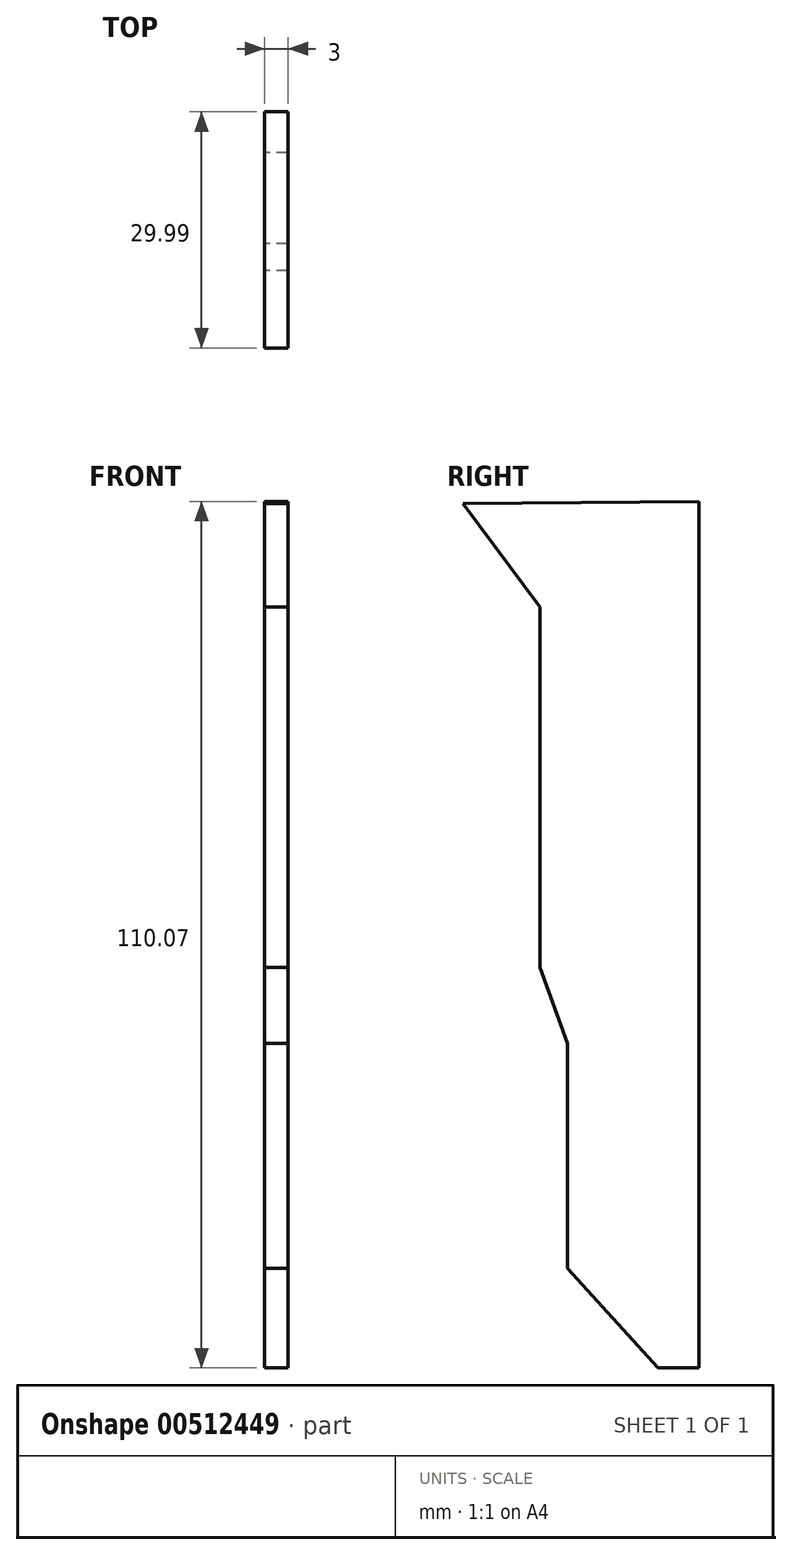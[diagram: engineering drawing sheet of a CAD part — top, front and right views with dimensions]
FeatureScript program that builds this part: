
annotation { "Feature Type Name" : "Feature", "Feature Type Description" : "" }
export const myFeature = defineFeature(function(context is Context, id is Id, definition is map)
    precondition{}
    {
        {
            var Q0;
            Q0=qCreatedBy(makeId("Right.planeOp"),FACE);
            var sketch = newSketch(context, id + "F0", { "sketchPlane" : qUnion([Q0])});
            skLineSegment(sketch, "E0", {"start": v(11.64, -33.52) * mm, "end": v(6.44, -33.52) * mm});
            skLineSegment(sketch, "E1", {"start": v(6.44, -33.52) * mm, "end": v(-5.09, -20.88) * mm});
            skLineSegment(sketch, "E2", {"start": v(-5.09, -20.88) * mm, "end": v(-5.09, -4.15) * mm});
            skLineSegment(sketch, "E3", {"start": v(-5.09, -4.15) * mm, "end": v(-5.09, 7.7) * mm});
            skLineSegment(sketch, "E4", {"start": v(-5.09, 7.7) * mm, "end": v(-8.52, 17.33) * mm});
            skLineSegment(sketch, "E5", {"start": v(-8.52, 17.33) * mm, "end": v(-8.52, 63.12) * mm});
            skLineSegment(sketch, "E6", {"start": v(-8.52, 63.12) * mm, "end": v(-18.35, 76.27) * mm});
            skLineSegment(sketch, "E7", {"start": v(11.64, -33.52) * mm, "end": v(11.64, 76.55) * mm});
            skLineSegment(sketch, "E8", {"start": v(11.64, 76.55) * mm, "end": v(-18.35, 76.27) * mm});
            skSolve(sketch);
        }
        {
            var Q0;
            Q0 = qSketchRegion(id + "F0", true);
            extrude(context, id + "F1", {"entities" : qUnion([Q0]), "depth" : 3 * mm});
        }
    });
